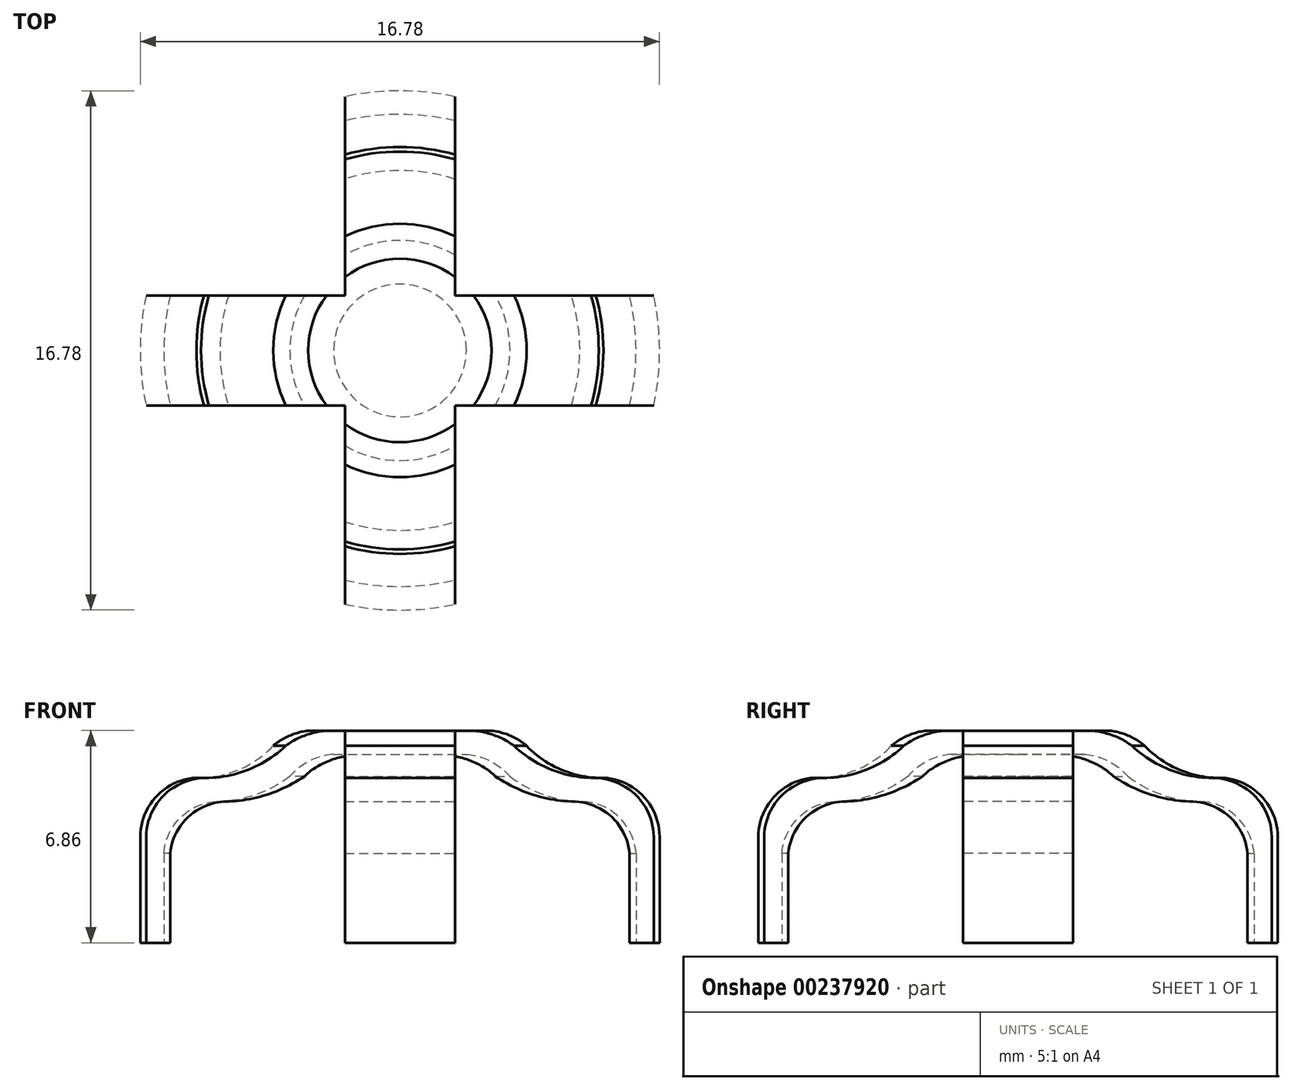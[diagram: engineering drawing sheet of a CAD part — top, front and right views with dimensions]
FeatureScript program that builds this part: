
annotation { "Feature Type Name" : "Feature", "Feature Type Description" : "" }
export const myFeature = defineFeature(function(context is Context, id is Id, definition is map)
    precondition{}
    {
        {
            var Q0;
            Q0=qCreatedBy(makeId("Front.planeOp"),FACE);
            var sketch = newSketch(context, id + "F0", { "sketchPlane" : qUnion([Q0])});
            skLineSegment(sketch, "E0", {"start": v(0, 6.86) * mm, "end": v(2.97, 6.86) * mm});
            skLineSegment(sketch, "E1", {"start": v(6.43, 5.33) * mm, "end": v(6.58, 5.33) * mm});
            skLineSegment(sketch, "E2", {"start": v(8.4, 3.42) * mm, "end": v(8.4, 0) * mm});
            skLineSegment(sketch, "E3", {"start": v(8.4, 0) * mm, "end": v(7.63, 0) * mm});
            skLineSegment(sketch, "E4", {"start": v(7.63, 0) * mm, "end": v(7.63, 2.89) * mm});
            skLineSegment(sketch, "E5", {"start": v(2.14, 6.1) * mm, "end": v(0, 6.1) * mm});
            skLineSegment(sketch, "E6", {"start": v(0, 0) * mm, "end": v(0, 10.27) * mm});
            skArc(sketch, "E7", {"start": v(4.1, 6.37) * mm, "mid": v(3.57, 6.7) * mm, "end": v(2.97, 6.86) * mm});
            skArc(sketch, "E8", {"start": v(3.56, 5.38) * mm, "mid": v(2.92, 5.88) * mm, "end": v(2.14, 6.1) * mm});
            skArc(sketch, "E9", {"start": v(4.1, 6.37) * mm, "mid": v(5.16, 5.62) * mm, "end": v(6.43, 5.33) * mm});
            skArc(sketch, "E10", {"start": v(3.56, 5.38) * mm, "mid": v(4.62, 4.8) * mm, "end": v(5.82, 4.57) * mm});
            skPoint(sketch, "E11.orphan", {"position": v(4, 4.57) * mm});
            skPoint(sketch, "E12.orphan", {"position": v(4.76, 5.33) * mm});
            skPoint(sketch, "E13.orphan", {"position": v(6.58, 5.33) * mm});
            skArc(sketch, "E14", {"start": v(8.4, 3.42) * mm, "mid": v(7.87, 4.74) * mm, "end": v(6.58, 5.33) * mm});
            skArc(sketch, "E15", {"start": v(7.63, 2.89) * mm, "mid": v(7.06, 4.09) * mm, "end": v(5.82, 4.57) * mm});
            skPoint(sketch, "E16.orphan", {"position": v(8.4, 5.33) * mm});
            skPoint(sketch, "E17.orphan", {"position": v(7.63, 4.57) * mm});
            skSolve(sketch);
        }
        {
            var Q0;
            Q0 = qSketchRegion(id + "F0", true);
            var Q1;
            Q1=sQuery(id+"F0.wireOp",EDGE,"E6");
            revolve(context, id + "F1", {"entities" : qUnion([Q0]), "axis" : qUnion([Q1]), "revolveType" : RevolveType.FULL});
        }
        {
            var Q0;
            Q0=qCreatedBy(makeId("Top.planeOp"),FACE);
            var sketch = newSketch(context, id + "F2", { "sketchPlane" : qUnion([Q0])});
            skPoint(sketch, "E18.middle", {"position": v(0, 0) * mm});
            skLineSegment(sketch, "E19.bottom", {"start": v(-1.78, -1.78) * mm, "end": v(-8.98, -1.78) * mm});
            skLineSegment(sketch, "E19.top", {"start": v(-1.78, -9.02) * mm, "end": v(-8.98, -9.02) * mm});
            skLineSegment(sketch, "E19.left", {"start": v(-1.78, -1.78) * mm, "end": v(-1.78, -9.02) * mm});
            skLineSegment(sketch, "E19.right", {"start": v(-8.98, -1.78) * mm, "end": v(-8.98, -9.02) * mm});
            skLineSegment(sketch, "E20.bottom", {"start": v(1.78, -1.78) * mm, "end": v(9.06, -1.78) * mm});
            skLineSegment(sketch, "E20.top", {"start": v(1.78, -9.56) * mm, "end": v(9.06, -9.56) * mm});
            skLineSegment(sketch, "E20.left", {"start": v(1.78, -1.78) * mm, "end": v(1.78, -9.56) * mm});
            skLineSegment(sketch, "E20.right", {"start": v(9.06, -1.78) * mm, "end": v(9.06, -9.56) * mm});
            skLineSegment(sketch, "E21.bottom", {"start": v(1.78, 1.78) * mm, "end": v(9.34, 1.78) * mm});
            skLineSegment(sketch, "E21.top", {"start": v(1.78, 9.06) * mm, "end": v(9.34, 9.06) * mm});
            skLineSegment(sketch, "E21.left", {"start": v(1.78, 1.78) * mm, "end": v(1.78, 9.06) * mm});
            skLineSegment(sketch, "E21.right", {"start": v(9.34, 1.78) * mm, "end": v(9.34, 9.06) * mm});
            skLineSegment(sketch, "E22.bottom", {"start": v(-1.78, 1.78) * mm, "end": v(-8.56, 1.78) * mm});
            skLineSegment(sketch, "E22.top", {"start": v(-1.78, 8.57) * mm, "end": v(-8.56, 8.57) * mm});
            skLineSegment(sketch, "E22.left", {"start": v(-1.78, 1.78) * mm, "end": v(-1.78, 8.57) * mm});
            skLineSegment(sketch, "E22.right", {"start": v(-8.56, 1.78) * mm, "end": v(-8.56, 8.57) * mm});
            skSolve(sketch);
        }
        {
            var Q0;
            Q0 = qSketchRegion(id + "F2", true);
            extrude(context, id + "F3", {"entities" : qUnion([Q0]), "operationType" : NewBodyOperationType.REMOVE, "depth" : 25.4 * mm});
        }
    });
